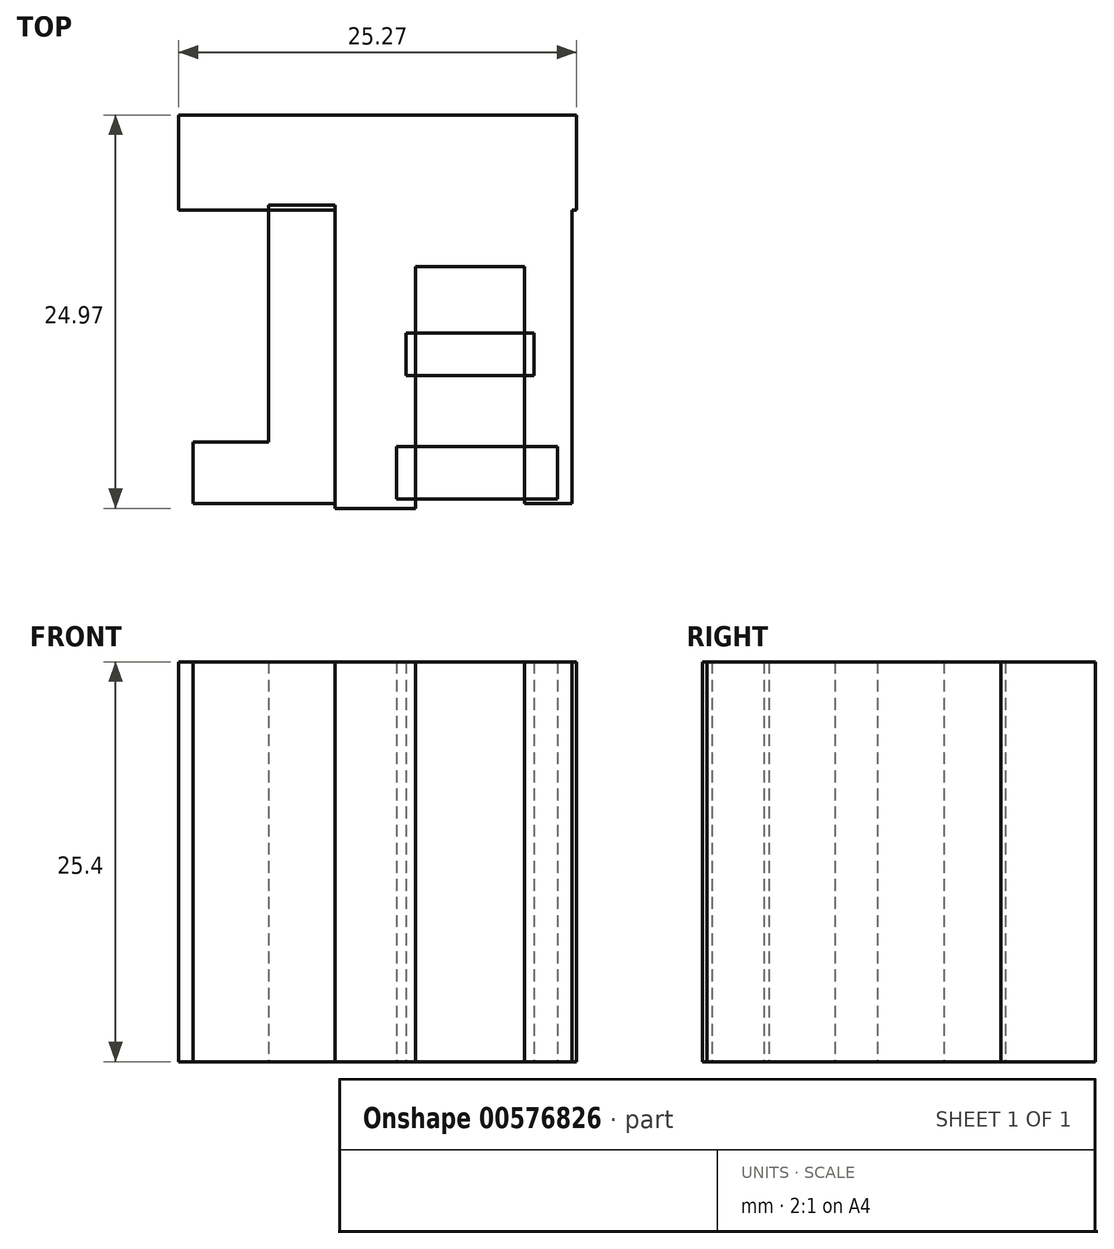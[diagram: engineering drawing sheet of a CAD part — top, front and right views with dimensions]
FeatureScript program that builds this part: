
annotation { "Feature Type Name" : "Feature", "Feature Type Description" : "" }
export const myFeature = defineFeature(function(context is Context, id is Id, definition is map)
    precondition{}
    {
        {
            var Q0;
            Q0=qCreatedBy(makeId("Top.planeOp"),FACE);
            var sketch = newSketch(context, id + "F0", { "sketchPlane" : qUnion([Q0])});
            skLineSegment(sketch, "E0.bottom", {"start": v(-9.84, 9.54) * mm, "end": v(15.56, 9.54) * mm});
            skLineSegment(sketch, "E0.top", {"start": v(-9.84, -15.86) * mm, "end": v(15.56, -15.86) * mm});
            skLineSegment(sketch, "E0.left", {"start": v(-9.84, 9.54) * mm, "end": v(-9.84, -15.86) * mm});
            skLineSegment(sketch, "E0.right", {"start": v(15.56, 9.54) * mm, "end": v(15.56, -15.86) * mm});
            skSolve(sketch);
        }
        {
            var Q0;
            Q0=makeQuery(id+"F0.imprint","IMPRINT",FACE,{"disambiguationData":[TD([[makeQuery(id+"F0.imprint","IMPRINT",EDGE,{"derivedFrom":sQuery(id+"F0.wireOp",EDGE,"E0.bottom")}),-1.0]])]});
            var sketch = newSketch(context, id + "F1", { "sketchPlane" : qUnion([Q0])});
            skLineSegment(sketch, "E1.bottom", {"start": v(-9.93, 9.63) * mm, "end": v(15.34, 9.63) * mm});
            skLineSegment(sketch, "E1.top", {"start": v(-9.93, 3.6) * mm, "end": v(15.34, 3.6) * mm});
            skLineSegment(sketch, "E1.left", {"start": v(-9.93, 9.63) * mm, "end": v(-9.93, 3.6) * mm});
            skLineSegment(sketch, "E1.right", {"start": v(15.34, 9.63) * mm, "end": v(15.34, 3.6) * mm});
            skSolve(sketch);
        }
        {
            var Q0;
            Q0 = qSketchRegion(id + "F1", true);
            extrude(context, id + "F2", {"entities" : qUnion([Q0]), "depth" : 25.4 * mm, "offsetDistance" : 25.4 * mm});
        }
        {
            var Q0;
            Q0=makeQuery(id+"F0.imprint","IMPRINT",FACE,{"disambiguationData":[TD([[makeQuery(id+"F0.imprint","IMPRINT",EDGE,{"derivedFrom":sQuery(id+"F0.wireOp",EDGE,"E0.bottom")}),-1.0]])]});
            var sketch = newSketch(context, id + "F3", { "sketchPlane" : qUnion([Q0])});
            skLineSegment(sketch, "E2.bottom", {"start": v(0, 3.91) * mm, "end": v(-4.21, 3.91) * mm});
            skLineSegment(sketch, "E2.top", {"start": v(0, -15.04) * mm, "end": v(-4.21, -15.04) * mm});
            skLineSegment(sketch, "E2.left", {"start": v(0, 3.91) * mm, "end": v(0, -15.04) * mm});
            skLineSegment(sketch, "E2.right", {"start": v(-4.21, 3.91) * mm, "end": v(-4.21, -15.04) * mm});
            skSolve(sketch);
        }
        {
            var Q0;
            Q0 = qSketchRegion(id + "F3", true);
            extrude(context, id + "F4", {"entities" : qUnion([Q0]), "depth" : 25.4 * mm, "offsetDistance" : 25.4 * mm});
        }
        {
            var Q0;
            Q0=makeQuery(id+"F0.imprint","IMPRINT",FACE,{"disambiguationData":[TD([[makeQuery(id+"F0.imprint","IMPRINT",EDGE,{"derivedFrom":sQuery(id+"F0.wireOp",EDGE,"E0.bottom")}),-1.0]])]});
            var sketch = newSketch(context, id + "F5", { "sketchPlane" : qUnion([Q0])});
            skLineSegment(sketch, "E3.bottom", {"start": v(0, -11.13) * mm, "end": v(-9.02, -11.13) * mm});
            skLineSegment(sketch, "E3.top", {"start": v(0, -15.04) * mm, "end": v(-9.02, -15.04) * mm});
            skLineSegment(sketch, "E3.left", {"start": v(0, -11.13) * mm, "end": v(0, -15.04) * mm});
            skLineSegment(sketch, "E3.right", {"start": v(-9.02, -11.13) * mm, "end": v(-9.02, -15.04) * mm});
            skSolve(sketch);
        }
        {
            var Q0;
            Q0 = qSketchRegion(id + "F5", true);
            extrude(context, id + "F6", {"entities" : qUnion([Q0]), "operationType" : NewBodyOperationType.ADD, "depth" : 25.4 * mm, "offsetDistance" : 25.4 * mm});
        }
        {
            var Q0;
            Q0=makeQuery(id+"F0.imprint","IMPRINT",FACE,{"disambiguationData":[TD([[makeQuery(id+"F0.imprint","IMPRINT",EDGE,{"derivedFrom":sQuery(id+"F0.wireOp",EDGE,"E0.bottom")}),-1.0]])]});
            var sketch = newSketch(context, id + "F7", { "sketchPlane" : qUnion([Q0])});
            skLineSegment(sketch, "E4.bottom", {"start": v(5.11, 3.91) * mm, "end": v(0, 3.91) * mm});
            skLineSegment(sketch, "E4.top", {"start": v(5.11, -15.34) * mm, "end": v(0, -15.34) * mm});
            skLineSegment(sketch, "E4.left", {"start": v(5.11, 3.91) * mm, "end": v(5.11, -15.34) * mm});
            skLineSegment(sketch, "E4.right", {"start": v(0, 3.91) * mm, "end": v(0, -15.34) * mm});
            skSolve(sketch);
        }
        {
            var Q0;
            Q0 = qSketchRegion(id + "F7", true);
            extrude(context, id + "F8", {"entities" : qUnion([Q0]), "depth" : 25.4 * mm, "offsetDistance" : 25.4 * mm});
        }
        {
            var Q0;
            Q0=makeQuery(id+"F0.imprint","IMPRINT",FACE,{"disambiguationData":[TD([[makeQuery(id+"F0.imprint","IMPRINT",EDGE,{"derivedFrom":sQuery(id+"F0.wireOp",EDGE,"E0.bottom")}),-1.0]])]});
            var sketch = newSketch(context, id + "F9", { "sketchPlane" : qUnion([Q0])});
            skLineSegment(sketch, "E5.bottom", {"start": v(3.6, 0) * mm, "end": v(15.04, 0) * mm});
            skLineSegment(sketch, "E5.top", {"start": v(3.6, 3.6) * mm, "end": v(15.04, 3.6) * mm});
            skLineSegment(sketch, "E5.left", {"start": v(3.6, 0) * mm, "end": v(3.6, 3.6) * mm});
            skLineSegment(sketch, "E5.right", {"start": v(15.04, 0) * mm, "end": v(15.04, 3.6) * mm});
            skSolve(sketch);
        }
        {
            var Q0;
            Q0 = qSketchRegion(id + "F9", true);
            extrude(context, id + "F10", {"entities" : qUnion([Q0]), "operationType" : NewBodyOperationType.ADD, "depth" : 25.4 * mm, "offsetDistance" : 25.4 * mm});
        }
        {
            var Q0;
            Q0=makeQuery(id+"F0.imprint","IMPRINT",FACE,{"disambiguationData":[TD([[makeQuery(id+"F0.imprint","IMPRINT",EDGE,{"derivedFrom":sQuery(id+"F0.wireOp",EDGE,"E0.bottom")}),-1.0]])]});
            var sketch = newSketch(context, id + "F11", { "sketchPlane" : qUnion([Q0])});
            skLineSegment(sketch, "E6.bottom", {"start": v(15.04, 3.3) * mm, "end": v(12.03, 3.3) * mm});
            skLineSegment(sketch, "E6.top", {"start": v(15.04, -15.04) * mm, "end": v(12.03, -15.04) * mm});
            skLineSegment(sketch, "E6.left", {"start": v(15.04, 3.3) * mm, "end": v(15.04, -15.04) * mm});
            skLineSegment(sketch, "E6.right", {"start": v(12.03, 3.3) * mm, "end": v(12.03, -15.04) * mm});
            skSolve(sketch);
        }
        {
            var Q0;
            Q0 = qSketchRegion(id + "F11", true);
            extrude(context, id + "F12", {"entities" : qUnion([Q0]), "operationType" : NewBodyOperationType.ADD, "depth" : 25.4 * mm, "offsetDistance" : 25.4 * mm});
        }
        {
            var Q0;
            Q0=makeQuery(id+"F0.imprint","IMPRINT",FACE,{"disambiguationData":[TD([[makeQuery(id+"F0.imprint","IMPRINT",EDGE,{"derivedFrom":sQuery(id+"F0.wireOp",EDGE,"E0.bottom")}),-1.0]])]});
            var sketch = newSketch(context, id + "F13", { "sketchPlane" : qUnion([Q0])});
            skLineSegment(sketch, "E7.bottom", {"start": v(12.63, -4.21) * mm, "end": v(4.51, -4.21) * mm});
            skLineSegment(sketch, "E7.top", {"start": v(12.63, -6.92) * mm, "end": v(4.51, -6.92) * mm});
            skLineSegment(sketch, "E7.left", {"start": v(12.63, -4.21) * mm, "end": v(12.63, -6.92) * mm});
            skLineSegment(sketch, "E7.right", {"start": v(4.51, -4.21) * mm, "end": v(4.51, -6.92) * mm});
            skSolve(sketch);
        }
        {
            var Q0;
            Q0 = qSketchRegion(id + "F13", true);
            extrude(context, id + "F14", {"entities" : qUnion([Q0]), "depth" : 25.4 * mm, "offsetDistance" : 25.4 * mm});
        }
        {
            var Q0;
            Q0=makeQuery(id+"F0.imprint","IMPRINT",FACE,{"disambiguationData":[TD([[makeQuery(id+"F0.imprint","IMPRINT",EDGE,{"derivedFrom":sQuery(id+"F0.wireOp",EDGE,"E0.bottom")}),-1.0]])]});
            var sketch = newSketch(context, id + "F15", { "sketchPlane" : qUnion([Q0])});
            skLineSegment(sketch, "E8.bottom", {"start": v(3.91, -14.74) * mm, "end": v(14.14, -14.74) * mm});
            skLineSegment(sketch, "E8.top", {"start": v(3.91, -11.43) * mm, "end": v(14.14, -11.43) * mm});
            skLineSegment(sketch, "E8.left", {"start": v(3.91, -14.74) * mm, "end": v(3.91, -11.43) * mm});
            skLineSegment(sketch, "E8.right", {"start": v(14.14, -14.74) * mm, "end": v(14.14, -11.43) * mm});
            skSolve(sketch);
        }
        {
            var Q0;
            Q0 = qSketchRegion(id + "F15", true);
            extrude(context, id + "F16", {"entities" : qUnion([Q0]), "depth" : 25.4 * mm, "offsetDistance" : 25.4 * mm});
        }
    });
